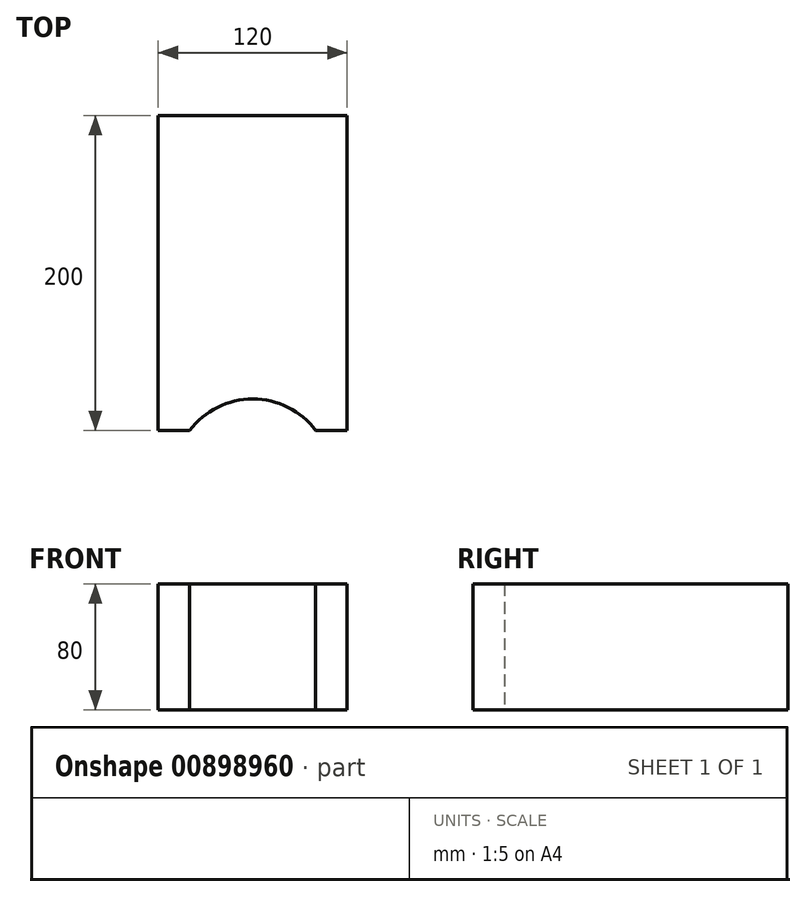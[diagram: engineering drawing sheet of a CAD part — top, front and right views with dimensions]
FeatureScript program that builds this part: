
annotation { "Feature Type Name" : "Feature", "Feature Type Description" : "" }
export const myFeature = defineFeature(function(context is Context, id is Id, definition is map)
    precondition{}
    {
        {
            var Q0;
            Q0=qCreatedBy(makeId("Top.planeOp"),FACE);
            var sketch = newSketch(context, id + "F0", { "sketchPlane" : qUnion([Q0])});
            skLineSegment(sketch, "E0.bottom", {"start": v(60, 100) * mm, "end": v(-60, 100) * mm});
            skLineSegment(sketch, "E0.left", {"start": v(60, 100) * mm, "end": v(60, -100) * mm});
            skLineSegment(sketch, "E0.right", {"start": v(-60, 100) * mm, "end": v(-60, -100) * mm});
            skPoint(sketch, "E0.middle", {"position": v(0, 0) * mm});
            skLineSegment(sketch, "E1", {"start": v(-60, -100) * mm, "end": v(-40, -100) * mm});
            skLineSegment(sketch, "E2", {"start": v(60, -100) * mm, "end": v(40, -100) * mm});
            skArc(sketch, "E3", {"start": v(40, -100) * mm, "mid": v(0, -80) * mm, "end": v(-40, -100) * mm});
            skSolve(sketch);
        }
        {
            var Q0;
            Q0=makeQuery(id+"F0.imprint","IMPRINT",FACE,{"disambiguationData":[TD([[makeQuery(id+"F0.imprint","IMPRINT",EDGE,{"derivedFrom":sQuery(id+"F0.wireOp",EDGE,"E0.bottom")}),1.0]])]});
            extrude(context, id + "F1", {"entities" : qUnion([Q0]), "depth" : 80 * mm, "offsetDistance" : 25 * mm});
        }
    });
